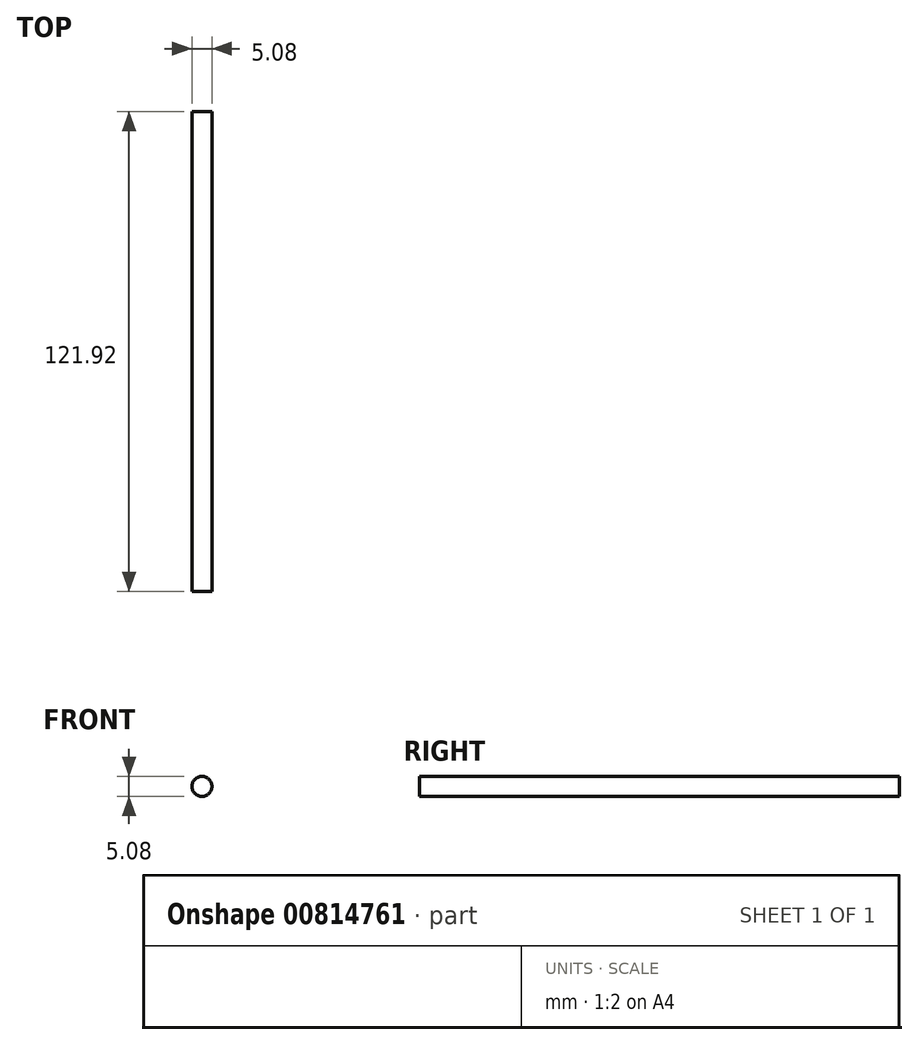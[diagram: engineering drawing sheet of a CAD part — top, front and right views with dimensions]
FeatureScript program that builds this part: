
annotation { "Feature Type Name" : "Feature", "Feature Type Description" : "" }
export const myFeature = defineFeature(function(context is Context, id is Id, definition is map)
    precondition{}
    {
        {
            var Q0;
            Q0=qCreatedBy(makeId("Front.planeOp"),FACE);
            var sketch = newSketch(context, id + "F0", { "sketchPlane" : qUnion([Q0])});
            skCircle(sketch, "E0", {"center": v(0, 0) * mm, "radius": 2.54 * mm});
            skSolve(sketch);
        }
        {
            var Q0;
            Q0 = qSketchRegion(id + "F0", true);
            extrude(context, id + "F1", {"entities" : qUnion([Q0]), "depth" : 121.92 * mm, "offsetDistance" : 25.4 * mm});
        }
    });
